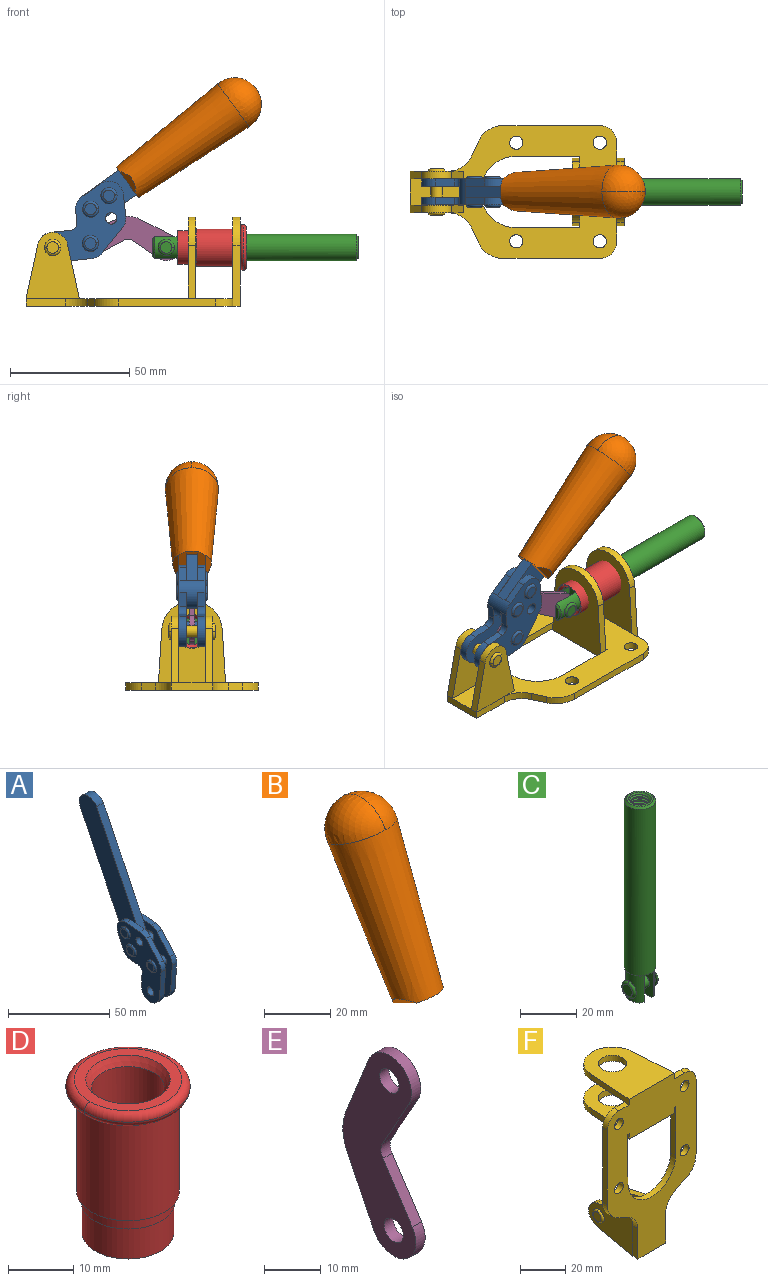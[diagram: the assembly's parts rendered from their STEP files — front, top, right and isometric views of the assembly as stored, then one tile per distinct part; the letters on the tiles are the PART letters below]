
ASSEMBLY  parts=6 mates=6
PART A: 59 faces, bbox 12.9x60.2x99.6 mm
  f0: torus R=2.39mm, axis (-1,0,0), area 14.9mm2, adj f20,f43,f51
  f1: torus R=2.39mm, axis (-1,0,0), area 14.9mm2, adj f19,f42,f51
  f2: torus R=2.39mm, axis (-1,0,0), area 14.9mm2, adj f18,f35,f51
  f3: torus R=2.39mm, axis (-1,0,0), area 14.9mm2, adj f14,f17,f23
  f4: torus R=2.39mm, axis (-1,0,0), area 14.9mm2, adj f13,f16,f23
  f5: torus R=2.39mm, axis (-1,0,0), area 14.9mm2, adj f12,f15,f23
  f6: cylinder r=2.39mm len=4.78mm, axis (1,0,0), area 46.5mm2, adj f48,f50,f51
  f7: cylinder r=2.39mm len=4.78mm, axis (1,0,0), area 46.5mm2, adj f50,f51
  f8: cylinder r=6.35mm len=12.68mm, axis (1,0,0), area 61.8mm2, adj f38,f39,f50,f51
  f9: cylinder r=2.39mm len=4.78mm, axis (-1,0,0), area 70.5mm2, adj f46,f50
  f10: cylinder r=2.39mm len=4.78mm, axis (-1,0,0), area 46.5mm2, adj f23,f45,f46
  f11: cylinder r=2.39mm len=4.78mm, axis (-1,0,0), area 46.5mm2, adj f23,f46
  f12: plane 4.78x4.78mm, normal (1,0,0), area 17.9mm2, adj f5,f15
  f13: plane 4.78x4.78mm, normal (1,0,0), area 17.9mm2, adj f4,f16
  f14: plane 4.78x4.78mm, normal (1,0,0), area 17.9mm2, adj f3,f17
  f15: torus R=2.39mm, axis (-1,0,0), area 14.9mm2, adj f5,f12,f23
  f16: torus R=2.39mm, axis (-1,0,0), area 14.9mm2, adj f4,f13,f23
  f17: torus R=2.39mm, axis (-1,0,0), area 14.9mm2, adj f3,f14,f23
  f18: plane 4.78x4.78mm, normal (-1,0,0), area 17.9mm2, adj f2,f35
  f19: plane 4.78x4.78mm, normal (-1,0,0), area 17.9mm2, adj f1,f42
  f20: plane 4.78x4.78mm, normal (-1,0,0), area 17.9mm2, adj f0,f43
  f21: plane 2.26x0.2mm, normal (1,0,0), area 0.2mm2, adj f31,f44
  f22: plane 2.26x0.2mm, normal (-1,0,0), area 0.2mm2, adj f41,f44
  f23: plane 39.37x30.77mm, normal (1,0,0), area 565.5mm2, adj f3,f4,f5,f10,f11,f15,f16,f17
  f24: cylinder r=6.1mm len=4.15mm, axis (-1,0,0), area 14.7mm2, adj f23,f25,f32,f46
  f25: plane 10.25x9.01mm, normal (0,-0.75,0.66), area 42.3mm2, adj f23,f24,f26,f46
  f26: cylinder r=6.35mm len=4.64mm, axis (-1,0,0), area 15.6mm2, adj f23,f25,f27,f46
  f27: plane 15.84x3.1mm, normal (0,-1,-0.07), area 49.2mm2, adj f23,f26,f28,f46
  f28: cylinder r=6.35mm len=12.68mm, axis (-1,0,0), area 61.8mm2, adj f23,f27,f29,f46
  f29: plane 8.11x3.1mm, normal (0,1,0.07), area 25.2mm2, adj f23,f28,f30,f46
  f30: cylinder r=3.05mm len=3.25mm, axis (-1,0,0), area 14.8mm2, adj f23,f29,f31,f46
  f31: plane 5.99x3.1mm, normal (0,0.07,-1), area 18.6mm2, adj f21,f23,f30,f44,f46
  f32: plane 9.5x3.1mm, normal (0,-0.07,1), area 29.5mm2, adj f23,f24,f33,f46,f47
  f33: cylinder r=6.1mm len=8.63mm, axis (-1,0,0), area 39.1mm2, adj f23,f32,f34,f47
  f34: plane 8.65x3.96mm, normal (0,0.91,-0.42), area 29.5mm2, adj f23,f33,f44,f47
  f35: torus R=2.39mm, axis (-1,0,0), area 14.9mm2, adj f2,f18,f51
  f36: plane 10.25x9.01mm, normal (0,-0.75,0.66), area 42.3mm2, adj f37,f49,f50,f51
  f37: cylinder r=6.35mm len=4.64mm, axis (1,0,0), area 15.6mm2, adj f36,f38,f50,f51
  f38: plane 15.84x3.1mm, normal (0,-1,-0.07), area 49.2mm2, adj f8,f37,f50,f51
  f39: plane 8.11x3.1mm, normal (0,1,0.07), area 25.2mm2, adj f8,f40,f50,f51
  f40: cylinder r=3.05mm len=3.25mm, axis (1,0,0), area 14.8mm2, adj f39,f41,f50,f51
  f41: plane 5.99x3.1mm, normal (0,0.07,-1), area 18.6mm2, adj f22,f40,f44,f50,f51
  f42: torus R=2.39mm, axis (-1,0,0), area 14.9mm2, adj f1,f19,f51
  f43: torus R=2.39mm, axis (-1,0,0), area 14.9mm2, adj f0,f20,f51
  f44: cylinder r=6.35mm len=12.12mm, axis (-1,0,0), area 128.9mm2, adj f21,f22,f23,f31,f34,f41,f46,f47
  f45: plane 2.65x1.35mm, normal (1,0,0), area 1mm2, adj f10,f55
  f46: plane 39.08x20.42mm, normal (-1,0,0), area 412.5mm2, adj f9,f10,f11,f24,f25,f26,f27,f28
  f47: plane 77.62x39.82mm, normal (1,0,0), area 850mm2, adj f32,f33,f34,f44,f53,f54,f55
  f48: plane 2.65x1.35mm, normal (-1,0,0), area 1mm2, adj f6,f55
  f49: cylinder r=6.1mm len=4.15mm, axis (1,0,0), area 14.7mm2, adj f36,f50,f51,f56
  f50: plane 39.08x20.42mm, normal (1,0,0), area 412.5mm2, adj f6,f7,f8,f9,f36,f37,f38,f39
  f51: plane 39.37x30.77mm, normal (-1,0,0), area 565.5mm2, adj f0,f1,f2,f6,f7,f8,f35,f36
  f52: plane 8.65x3.96mm, normal (0,0.91,-0.42), area 29.5mm2, adj f44,f51,f57,f58
  f53: plane 68.49x33.4mm, normal (0,0.9,-0.44), area 358.1mm2, adj f44,f47,f54,f58
  f54: cylinder r=6.35mm len=12.06mm, axis (1,0,0), area 93.7mm2, adj f47,f53,f55,f58
  f55: plane 68.49x33.4mm, normal (0,-0.9,0.44), area 358.1mm2, adj f44,f45,f46,f47,f48,f50,f54,f58
  f56: plane 9.5x3.1mm, normal (0,-0.07,1), area 29.5mm2, adj f49,f50,f51,f57,f58
  f57: cylinder r=6.1mm len=8.63mm, axis (1,0,0), area 39.1mm2, adj f51,f52,f56,f58
  f58: plane 77.62x39.82mm, normal (-1,0,0), area 850mm2, adj f44,f52,f53,f54,f55,f56,f57
PART B: 11 faces, bbox 22.3x42.6x64.5 mm
  f0: sphere r=11.13mm, area 411.4mm2, adj f1,f8
  f1: cone r=11.11mm half-angle=3.3deg, axis (0,0.44,0.9), area 3251.8mm2, adj f0,f7,f8,f9,f10
  f2: cylinder r=6.16mm len=11.7mm, axis (1,0,0), area 89.5mm2, adj f3,f4,f5,f6
  f3: plane 60.23x36.75mm, normal (-1,0,0), area 763.6mm2, adj f2,f4,f6,f10
  f4: plane 51.37x25.05mm, normal (0,0.9,-0.44), area 264.2mm2, adj f2,f3,f5,f10
  f5: plane 60.23x36.75mm, normal (1,0,0), area 763.6mm2, adj f2,f4,f6,f10
  f6: plane 51.37x25.05mm, normal (0,-0.9,0.44), area 264.2mm2, adj f2,f3,f5,f10
  f7: plane 9.95x5.95mm, normal (0.71,-0.31,-0.64), area 25.8mm2, adj f1,f10
  f8: sphere r=11.13mm, area 411.4mm2, adj f0,f1
  f9: plane 9.95x5.95mm, normal (-0.71,-0.31,-0.64), area 25.8mm2, adj f1,f10
  f10: plane 14.27x11.38mm, normal (0,-0.44,-0.9), area 106.7mm2, adj f1,f3,f4,f5,f6,f7,f9
PART C: 48 faces, bbox 12.6x11.1x86.1 mm
  f0: torus R=2.41mm, axis (-1,0,0), area 15mm2, adj f30,f32,f34
  f1: torus R=2.41mm, axis (-1,0,0), area 15mm2, adj f29,f31,f33
  f2: cylinder r=5.54mm len=72.39mm, axis (0,0,1), area 2518.5mm2, adj f3,f4,f42,f43
  f3: cone r=5.54mm half-angle=45deg, axis (0,0,1), area 7.6mm2, adj f2,f5,f41
  f4: cone r=5.54mm half-angle=45deg, axis (0,0,-1), area 34.9mm2, adj f2,f39
  f5: cylinder r=5.08mm len=11.48mm, axis (0,0,1), area 108.3mm2, adj f3,f7,f8,f41
  f6: cylinder r=2.41mm len=4.83mm, axis (-1,0,0), area 71.2mm2, adj f40,f41
  f7: cylinder r=2.41mm len=4.83mm, axis (-1,0,0), area 7.6mm2, adj f5,f34
  f8: cone r=5.08mm half-angle=45deg, axis (0,0,1), area 10.6mm2, adj f5,f37,f41
  f9: cone r=3.98mm half-angle=45deg, axis (0,0,1), area 17.6mm2, adj f27,f39,f45,f46,f47
  f10: cylinder r=2.41mm len=4.83mm, axis (-1,0,0), area 7.6mm2, adj f33,f38
  f11: cylinder r=3.2mm len=6.4mm, axis (0,0,1), area 78.4mm2, adj f12,f28,f44,f45,f47
  f12: cylinder r=3.2mm len=6.4mm, axis (0,0,1), area 10.5mm2, adj f11,f13,f45,f47
  f13: cylinder r=3.2mm len=6.4mm, axis (0,0,1), area 10.5mm2, adj f12,f14,f45,f47
  f14: cylinder r=3.2mm len=6.4mm, axis (0,0,1), area 10.5mm2, adj f13,f15,f45,f47
  f15: cylinder r=3.2mm len=6.4mm, axis (0,0,1), area 10.5mm2, adj f14,f16,f45,f47
  f16: cylinder r=3.2mm len=6.4mm, axis (0,0,1), area 10.5mm2, adj f15,f17,f45,f47
  f17: cylinder r=3.2mm len=6.4mm, axis (0,0,1), area 10.5mm2, adj f16,f18,f45,f47
  f18: cylinder r=3.2mm len=6.4mm, axis (0,0,1), area 10.5mm2, adj f17,f19,f45,f47
  f19: cylinder r=3.2mm len=6.4mm, axis (0,0,1), area 10.5mm2, adj f18,f20,f45,f47
  f20: cylinder r=3.2mm len=6.4mm, axis (0,0,1), area 10.5mm2, adj f19,f21,f45,f47
  f21: cylinder r=3.2mm len=6.4mm, axis (0,0,1), area 10.5mm2, adj f20,f22,f45,f47
  f22: cylinder r=3.2mm len=6.4mm, axis (0,0,1), area 10.5mm2, adj f21,f23,f45,f47
  f23: cylinder r=3.2mm len=6.4mm, axis (0,0,1), area 10.5mm2, adj f22,f24,f45,f47
  f24: cylinder r=3.2mm len=6.4mm, axis (0,0,1), area 10.5mm2, adj f23,f25,f45,f47
  f25: cylinder r=3.2mm len=6.4mm, axis (0,0,1), area 10.5mm2, adj f24,f26,f45,f47
  f26: cylinder r=3.2mm len=6.4mm, axis (0,0,1), area 10.5mm2, adj f25,f27,f45,f47
  f27: cylinder r=3.2mm len=6.4mm, axis (0,0,1), area 7.4mm2, adj f9,f26,f45,f47
  f28: cone r=3.2mm half-angle=60deg, axis (0,0,1), area 37.2mm2, adj f11
  f29: plane 4.83x4.83mm, normal (-1,0,0), area 18.3mm2, adj f1,f31
  f30: plane 4.83x4.83mm, normal (1,0,0), area 18.3mm2, adj f0,f32
  f31: torus R=2.41mm, axis (-1,0,0), area 15mm2, adj f1,f29,f33
  f32: torus R=2.41mm, axis (-1,0,0), area 15mm2, adj f0,f30,f34
  f33: plane 6.83x6.83mm, normal (1,0,0), area 18.3mm2, adj f1,f10,f31
  f34: plane 6.83x6.83mm, normal (-1,0,0), area 18.3mm2, adj f0,f7,f32
  f35: cone r=5.08mm half-angle=45deg, axis (0,0,1), area 10.6mm2, adj f36,f38,f40
  f36: plane 7.25x1.97mm, normal (0,0,-1), area 10mm2, adj f35,f40
  f37: plane 7.25x1.97mm, normal (0,0,-1), area 10mm2, adj f8,f41
  f38: cylinder r=5.08mm len=11.48mm, axis (0,0,1), area 108.3mm2, adj f10,f35,f40,f42
  f39: plane 9.55x9.55mm, normal (0,0,1), area 22mm2, adj f4,f9
  f40: plane 12.76x10.09mm, normal (1,0,0), area 95.7mm2, adj f6,f35,f36,f38,f42,f43
  f41: plane 12.76x10.09mm, normal (-1,0,0), area 95.7mm2, adj f3,f5,f6,f8,f37,f43
  f42: cone r=5.54mm half-angle=45deg, axis (0,0,1), area 7.6mm2, adj f2,f38,f40
  f43: plane 11.07x4.7mm, normal (0,0,-1), area 50.4mm2, adj f2,f40,f41
  f44: plane 0.89x0.62mm, normal (-1,0,0), area 0.3mm2, adj f11,f45,f46,f47
  f45: bspline ~24.8x7.63mm, area 266.6mm2, adj f9,f11,f12,f13,f14,f15,f16,f17
  f46: bspline ~24.87x7.63mm, area 73.6mm2, adj f9,f44,f45,f47
  f47: bspline ~24.98x7.63mm, area 272.5mm2, adj f9,f11,f12,f13,f14,f15,f16,f17
PART D: 15 faces, bbox 20.6x20.6x28.7 mm
  f0: torus R=8.26mm, axis (0,0,1), area 56.8mm2, adj f1,f10,f12
  f1: torus R=8.26mm, axis (0,0,1), area 56.8mm2, adj f0,f6,f13
  f2: cylinder r=5.59mm len=25.91mm, axis (0,0,1), area 909.6mm2, adj f3,f4
  f3: cone r=6.86mm half-angle=45deg, axis (0,0,-1), area 70.2mm2, adj f2,f14
  f4: cone r=6.47mm half-angle=30deg, axis (0,0,1), area 66.7mm2, adj f2,f13
  f5: cylinder r=7.04mm len=14.07mm, axis (0,0,1), area 252.6mm2, adj f11,f14
  f6: torus R=8.26mm, axis (0,0,1), area 56.8mm2, adj f1,f12,f13
  f7: cylinder r=7.16mm len=14.33mm, axis (0,0,1), area 91.5mm2, adj f9,f11
  f8: cylinder r=7.86mm len=18.42mm, axis (0,0,1), area 909.6mm2, adj f9,f10
  f9: plane 15.72x15.72mm, normal (0,0,-1), area 33mm2, adj f7,f8
  f10: plane 16.51x16.51mm, normal (0,0,-1), area 19.9mm2, adj f0,f8,f12
  f11: plane 14.33x14.33mm, normal (0,0,-1), area 5.7mm2, adj f5,f7
  f12: torus R=8.26mm, axis (0,0,1), area 56.8mm2, adj f0,f6,f10
  f13: plane 16.51x16.51mm, normal (0,0,1), area 82.7mm2, adj f1,f4,f6
  f14: plane 14.07x14.07mm, normal (0,0,-1), area 7.8mm2, adj f3,f5
PART E: 12 faces, bbox 2.3x18.2x42.8 mm
  f0: cylinder r=2.4mm len=4.8mm, axis (1,0,0), area 34.9mm2, adj f4,f11
  f1: cylinder r=10.41mm len=8.47mm, axis (1,0,0), area 20.2mm2, adj f4,f9,f10,f11
  f2: cylinder r=3.05mm len=3.16mm, axis (1,0,0), area 7.7mm2, adj f4,f6,f7,f11
  f3: cylinder r=2.4mm len=4.8mm, axis (1,0,0), area 34.9mm2, adj f4,f11
  f4: plane 42.81x18.23mm, normal (-1,0,0), area 414.1mm2, adj f0,f1,f2,f3,f5,f6,f7,f8
  f5: cylinder r=5.54mm len=10.67mm, axis (1,0,0), area 41.8mm2, adj f4,f6,f10,f11
  f6: plane 11.66x6.53mm, normal (0,-0.87,-0.49), area 30.9mm2, adj f2,f4,f5,f11
  f7: plane 11.17x7.33mm, normal (0,-0.84,0.55), area 30.9mm2, adj f2,f4,f8,f11
  f8: cylinder r=5.54mm len=10.51mm, axis (1,0,0), area 41.8mm2, adj f4,f7,f9,f11
  f9: plane 13.67x6.67mm, normal (0,0.9,-0.44), area 35.1mm2, adj f1,f4,f8,f11
  f10: plane 14.1x5.7mm, normal (0,0.93,0.37), area 35.1mm2, adj f1,f4,f5,f11
  f11: plane 42.81x18.23mm, normal (1,0,0), area 414.1mm2, adj f0,f1,f2,f3,f5,f6,f7,f8
PART F: 55 faces, bbox 55.7x37.4x89.8 mm
  f0: torus R=2.41mm, axis (-1,0,0), area 15mm2, adj f11,f15,f25
  f1: torus R=2.41mm, axis (-1,0,0), area 15mm2, adj f10,f12,f22
  f2: cylinder r=2.78mm len=5.56mm, axis (0,-1,0), area 54.2mm2, adj f30,f54
  f3: cylinder r=14.99mm len=29.97mm, axis (0,-1,0), area 145.9mm2, adj f30,f49,f53,f54
  f4: cylinder r=2.78mm len=5.56mm, axis (0,-1,0), area 54.2mm2, adj f30,f54
  f5: cylinder r=2.78mm len=5.56mm, axis (0,-1,0), area 54.2mm2, adj f30,f54
  f6: cylinder r=2.78mm len=5.56mm, axis (0,-1,0), area 54.2mm2, adj f30,f54
  f7: cylinder r=6.35mm len=12.7mm, axis (0,0,1), area 123.6mm2, adj f27,f51
  f8: cylinder r=6.35mm len=12.7mm, axis (0,0,-1), area 124.7mm2, adj f21,f35
  f9: cylinder r=2.41mm len=11.18mm, axis (-1,0,0), area 169.4mm2, adj f16,f19
  f10: plane 4.83x4.83mm, normal (1,0,0), area 18.3mm2, adj f1,f12
  f11: plane 4.83x4.83mm, normal (-1,0,0), area 18.3mm2, adj f0,f15
  f12: torus R=2.41mm, axis (-1,0,0), area 15mm2, adj f1,f10,f22
  f13: cylinder r=6.35mm len=12.41mm, axis (1,0,0), area 53.4mm2, adj f18,f19,f22,f23
  f14: cylinder r=6.35mm len=12.41mm, axis (-1,0,0), area 53.4mm2, adj f16,f17,f24,f25
  f15: torus R=2.41mm, axis (-1,0,0), area 15mm2, adj f0,f11,f25
  f16: plane 27.86x22.35mm, normal (1,0,0), area 425.4mm2, adj f9,f14,f17,f24,f30
  f17: plane 22.86x4.97mm, normal (0,0.21,0.98), area 72.5mm2, adj f14,f16,f25,f30
  f18: plane 22.86x4.97mm, normal (0,0.21,0.98), area 72.5mm2, adj f13,f19,f22,f30
  f19: plane 27.86x22.35mm, normal (-1,0,0), area 425.4mm2, adj f9,f13,f18,f23,f30
  f20: cylinder r=12.7mm len=25.35mm, axis (0,0,-1), area 119.8mm2, adj f21,f34,f35,f36
  f21: plane 34.21x28.07mm, normal (0,0,-1), area 702.4mm2, adj f8,f20,f30,f34,f36
  f22: plane 27.96x22.45mm, normal (1,0,0), area 407.2mm2, adj f1,f12,f13,f18,f23,f30,f42,f43
  f23: plane 22.86x4.97mm, normal (0,0.21,-0.98), area 72.5mm2, adj f13,f19,f22,f44
  f24: plane 22.86x4.97mm, normal (0,0.21,-0.98), area 72.5mm2, adj f14,f16,f25,f44
  f25: plane 27.86x22.35mm, normal (-1,0,0), area 407.1mm2, adj f0,f14,f15,f17,f24,f30,f45,f46
  f26: plane 3.1x0.95mm, normal (0,0,-1), area 2.7mm2, adj f30,f49,f50,f54
  f27: plane 34.21x28.07mm, normal (0,0,1), area 702.4mm2, adj f7,f28,f30,f50,f52
  f28: cylinder r=12.7mm len=25.35mm, axis (0,0,1), area 118.8mm2, adj f27,f50,f51,f52
  f29: plane 3.1x0.95mm, normal (0,0,-1), area 2.7mm2, adj f30,f52,f53,f54
  f30: plane 86.54x55.63mm, normal (0,1,0), area 2362.9mm2, adj f2,f3,f4,f5,f6,f16,f17,f18
  f31: plane 40.56x3.1mm, normal (-1,0,0), area 125.7mm2, adj f30,f32,f48,f54
  f32: cylinder r=7.11mm len=7.11mm, axis (0,-1,0), area 34.6mm2, adj f30,f31,f33,f54
  f33: plane 6.67x3.1mm, normal (0,0,1), area 20.4mm2, adj f30,f32,f34,f54
  f34: plane 25.39x3.13mm, normal (-1,0.06,0), area 79.5mm2, adj f20,f21,f33,f35,f54
  f35: plane 37.31x28.45mm, normal (0,0,1), area 789.9mm2, adj f8,f20,f34,f36,f54
  f36: plane 25.39x3.13mm, normal (1,0.06,0), area 79.5mm2, adj f20,f21,f35,f37,f54
  f37: plane 6.67x3.1mm, normal (0,0,1), area 20.4mm2, adj f30,f36,f38,f54
  f38: cylinder r=7.11mm len=7.11mm, axis (0,-1,0), area 34.6mm2, adj f30,f37,f39,f54
  f39: plane 40.56x3.1mm, normal (1,0,0), area 125.7mm2, adj f30,f38,f40,f54
  f40: cylinder r=11.18mm len=10.16mm, axis (0,-1,0), area 39.5mm2, adj f30,f39,f41,f54
  f41: plane 6.09x3.1mm, normal (0.42,0,-0.91), area 20.8mm2, adj f30,f40,f42,f54
  f42: cylinder r=11.18mm len=9.41mm, axis (0,-1,0), area 37.2mm2, adj f22,f30,f41,f43,f54
  f43: plane 16.5x3.1mm, normal (1,0,0), area 51.1mm2, adj f22,f42,f44,f54
  f44: plane 17.37x3.1mm, normal (0,0,-1), area 53.8mm2, adj f23,f24,f30,f43,f45,f54
  f45: plane 16.5x3.1mm, normal (-1,0,0), area 51.1mm2, adj f25,f44,f46,f54
  f46: cylinder r=11.18mm len=9.41mm, axis (0,-1,0), area 37.2mm2, adj f25,f30,f45,f47,f54
  f47: plane 6.09x3.1mm, normal (-0.42,0,-0.91), area 20.8mm2, adj f30,f46,f48,f54
  f48: cylinder r=11.18mm len=10.16mm, axis (0,-1,0), area 39.5mm2, adj f30,f31,f47,f54
  f49: plane 26.54x3.1mm, normal (-1,0,0), area 82.3mm2, adj f3,f26,f30,f54
  f50: plane 25.39x3.1mm, normal (1,0.06,0), area 78.8mm2, adj f26,f27,f28,f51,f54
  f51: plane 37.31x28.45mm, normal (0,0,-1), area 789.9mm2, adj f7,f28,f50,f52,f54
  f52: plane 25.39x3.1mm, normal (-1,0.06,0), area 78.8mm2, adj f27,f28,f29,f51,f54
  f53: plane 26.54x3.1mm, normal (1,0,0), area 82.3mm2, adj f3,f29,f30,f54
  f54: plane 89.66x55.63mm, normal (0,-1,0), area 2678.5mm2, adj f2,f3,f4,f5,f6,f26,f29,f31
PLACE A rot(axis=(0.54,0.54,0.64),114.4deg) t=(-31.69,6.52,6.07)mm
PLACE B rot(axis=(0.54,0.54,0.64),114.4deg) t=(-31.69,6.56,6.07)mm
PLACE C rot(axis=(-0.58,0.58,-0.58),120deg) t=(-35.55,6.52,49.35)mm
PLACE D rot(axis=(0,1,0),90deg) t=(-35.47,-18.09,24.74)mm
PLACE E rot(axis=(0.59,0.59,0.54),122.9deg) t=(-37.63,6.52,1.56)mm
PLACE F rot(axis=(0.58,0.58,0.58),120deg) t=(-35.47,6.52,0.12)mm fixed
MATE fastened D.f2 <-> F.f7  axis (-1,0,0) through (10.92,6.52,24.74)mm
MATE revolute E.f5 <-> C.f6  axis (0,1,0) through (-20.07,6.52,24.74)mm
MATE fastened B.f2 <-> A.f54  axis (0,-1,0) through (9.92,8.87,85.54)mm
MATE revolute F.f0 <-> A.f7  axis (0,-1,0) through (-67.57,6.52,24.74)mm
MATE slider C.f2 <-> D.f2  axis (1,0,0) through (23.24,6.52,24.74)mm
MATE revolute E.f3 <-> A.f4  axis (0,1,0) through (-51.78,6.52,26.39)mm
